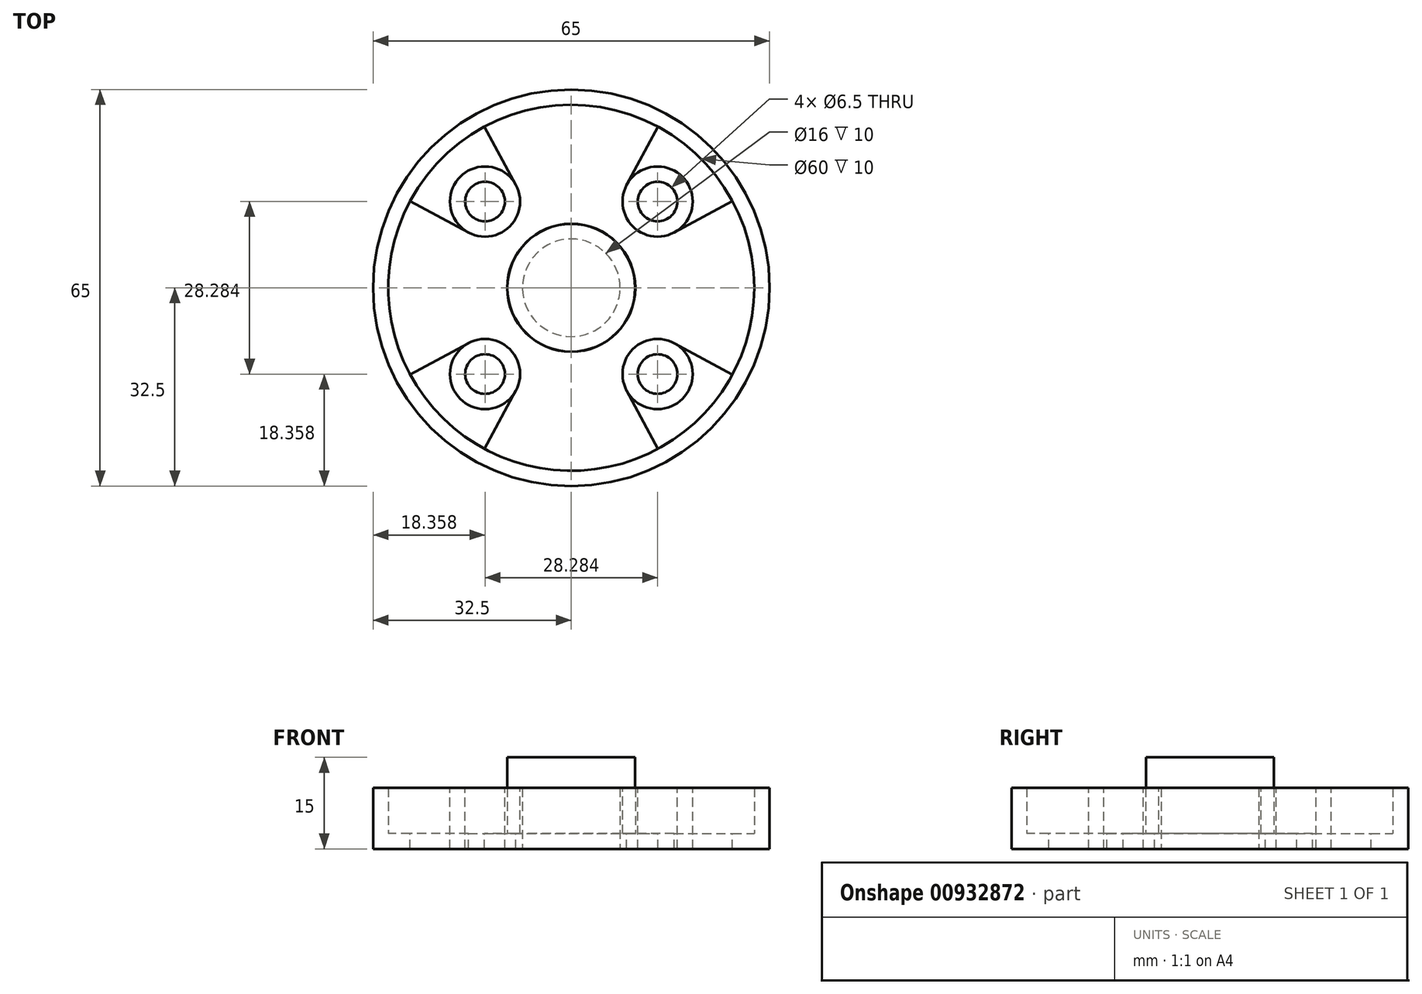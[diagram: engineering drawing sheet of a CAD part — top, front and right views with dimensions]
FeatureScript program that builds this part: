
annotation { "Feature Type Name" : "Feature", "Feature Type Description" : "" }
export const myFeature = defineFeature(function(context is Context, id is Id, definition is map)
    precondition{}
    {
        {
            var Q0;
            Q0=qCreatedBy(makeId("Top.planeOp"),FACE);
            var sketch = newSketch(context, id + "F0", { "sketchPlane" : qUnion([Q0])});
            skCircle(sketch, "E0", {"center": v(0, 0) * mm, "radius": 32.5 * mm});
            skSolve(sketch);
        }
        {
            var Q0;
            Q0=qSketchRegion(id+"F0",true);
            extrude(context, id + "F1", {"entities" : qUnion([Q0]), "depth" : 10 * mm, "offsetDistance" : 25 * mm});
        }
        {
            var Q0;
            Q0=qCreatedBy(makeId("Top.planeOp"),FACE);
            var sketch = newSketch(context, id + "F2", { "sketchPlane" : qUnion([Q0])});
            skCircle(sketch, "E1", {"center": v(0, 0) * mm, "radius": 8 * mm});
            skSolve(sketch);
        }
        {
            var Q0;
            Q0=qSketchRegion(id+"F2",true);
            extrude(context, id + "F3", {"entities" : qUnion([Q0]), "operationType" : NewBodyOperationType.REMOVE, "depth" : 25 * mm, "offsetDistance" : 25 * mm});
        }
        {
            var Q0;
            Q0=makeQuery(id+"F1.opExtrude","CAP_FACE",FACE,{"disambiguationData":[OSD([sQuery(id+"F0.wireOp",EDGE,"E0")])],"isStart":false});
            var sketch = newSketch(context, id + "F4", { "sketchPlane" : qUnion([Q0])});
            skCircle(sketch, "E2", {"center": v(-14.14, 14.14) * mm, "radius": 3.25 * mm});
            skCircle(sketch, "E3.MirrorC", {"center": v(-14.14, -14.14) * mm, "radius": 3.25 * mm});
            skCircle(sketch, "E4.MirrorC", {"center": v(14.14, 14.14) * mm, "radius": 3.25 * mm});
            skCircle(sketch, "E5.MirrorC", {"center": v(14.14, -14.14) * mm, "radius": 3.25 * mm});
            skSolve(sketch);
        }
        {
            var Q0;
            Q0=qSketchRegion(id+"F4",true);
            extrude(context, id + "F5", {"entities" : qUnion([Q0]), "operationType" : NewBodyOperationType.REMOVE, "oppositeDirection" : true, "depth" : 25 * mm, "offsetDistance" : 25 * mm});
        }
        {
            var Q0;
            Q0=makeQuery(id+"F1.opExtrude","CAP_FACE",FACE,{"disambiguationData":[OSD([sQuery(id+"F0.wireOp",EDGE,"E0")])],"isStart":false});
            shell(context, id + "F6", {"entities" : qUnion([Q0]), "thickness" : 2.5 * mm});
        }
        {
            var Q0;
            {var subQ0=sQuery(id+"F0.wireOp",EDGE,"E0");Q0=makeQuery(id+"F6.opShell","OFFSET_FACE",FACE,{"disambiguationData":[OSD([subQ0]),TDD([makeQuery(id+"F1.opExtrude","CAP_FACE",FACE,{"disambiguationData":[OSD([subQ0])],"isStart":true})])]});}
            var sketch = newSketch(context, id + "F7", { "sketchPlane" : qUnion([Q0])});
            skLineSegment(sketch, "E6", {"start": v(16.87, 9.08) * mm, "end": v(26.42, 14.22) * mm});
            skLineSegment(sketch, "E7", {"start": v(9.08, 16.87) * mm, "end": v(14.22, 26.42) * mm});
            skLineSegment(sketch, "E8.MirrorCS", {"start": v(-9.08, 16.87) * mm, "end": v(-14.22, 26.42) * mm});
            skLineSegment(sketch, "E9.MirrorCS", {"start": v(-16.87, 9.08) * mm, "end": v(-26.42, 14.22) * mm});
            skLineSegment(sketch, "E10.MirrorCS", {"start": v(16.87, -9.08) * mm, "end": v(26.42, -14.22) * mm});
            skLineSegment(sketch, "E11.MirrorCS", {"start": v(9.08, -16.87) * mm, "end": v(14.22, -26.42) * mm});
            skLineSegment(sketch, "E12.MirrorCS", {"start": v(-16.87, -9.08) * mm, "end": v(-26.42, -14.22) * mm});
            skLineSegment(sketch, "E13.MirrorCS", {"start": v(-9.08, -16.87) * mm, "end": v(-14.22, -26.42) * mm});
            skSolve(sketch);
        }
        {
            var Q0;
            Q0=qSketchRegion(id+"F7",true);
            var Q1;
            {var subQ0=sQuery(id+"F7.wireOp",EDGE,"E6");Q1=makeQuery(id+"F7.imprint","IMPRINT",FACE,{"disambiguationData":[TD([[makeQuery(id+"F7.imprint","IMPRINT",EDGE,{"derivedFrom":subQ0}),1.0]])]});}
            var Q2;
            {var subQ0=sQuery(id+"F7.wireOp",EDGE,"E8.MirrorCS");Q2=makeQuery(id+"F7.imprint","IMPRINT",FACE,{"disambiguationData":[TD([[makeQuery(id+"F7.imprint","IMPRINT",EDGE,{"derivedFrom":subQ0}),1.0]])]});}
            var Q3;
            {var subQ0=sQuery(id+"F7.wireOp",EDGE,"E10.MirrorCS");Q3=makeQuery(id+"F7.imprint","IMPRINT",FACE,{"disambiguationData":[TD([[makeQuery(id+"F7.imprint","IMPRINT",EDGE,{"derivedFrom":subQ0}),-1.0]])]});}
            var Q4;
            {var subQ0=sQuery(id+"F7.wireOp",EDGE,"E12.MirrorCS");Q4=makeQuery(id+"F7.imprint","IMPRINT",FACE,{"disambiguationData":[TD([[makeQuery(id+"F7.imprint","IMPRINT",EDGE,{"derivedFrom":subQ0}),1.0]])]});}
            extrude(context, id + "F8", {"entities" : qUnion([Q0, Q1, Q2, Q3, Q4]), "operationType" : NewBodyOperationType.REMOVE, "oppositeDirection" : true, "depth" : 25 * mm, "offsetDistance" : 25 * mm});
        }
        {
            var Q0;
            {var subQ0=sQuery(id+"F0.wireOp",EDGE,"E0");Q0=makeQuery(id+"F6.opShell","OFFSET_FACE",FACE,{"disambiguationData":[OSD([subQ0]),TDD([makeQuery(id+"F1.opExtrude","CAP_FACE",FACE,{"disambiguationData":[OSD([subQ0])],"isStart":false})]),OD(1.0)]});}
            var sketch = newSketch(context, id + "F9", { "sketchPlane" : qUnion([Q0])});
            skCircle(sketch, "E14", {"center": v(0, 0) * mm, "radius": 10.47 * mm});
            skSolve(sketch);
        }
        {
            var Q0;
            Q0 = qSketchRegion(id + "F9", true);
            extrude(context, id + "F10", {"entities" : qUnion([Q0]), "operationType" : NewBodyOperationType.ADD, "depth" : 5 * mm, "offsetDistance" : 25 * mm});
        }
    });
